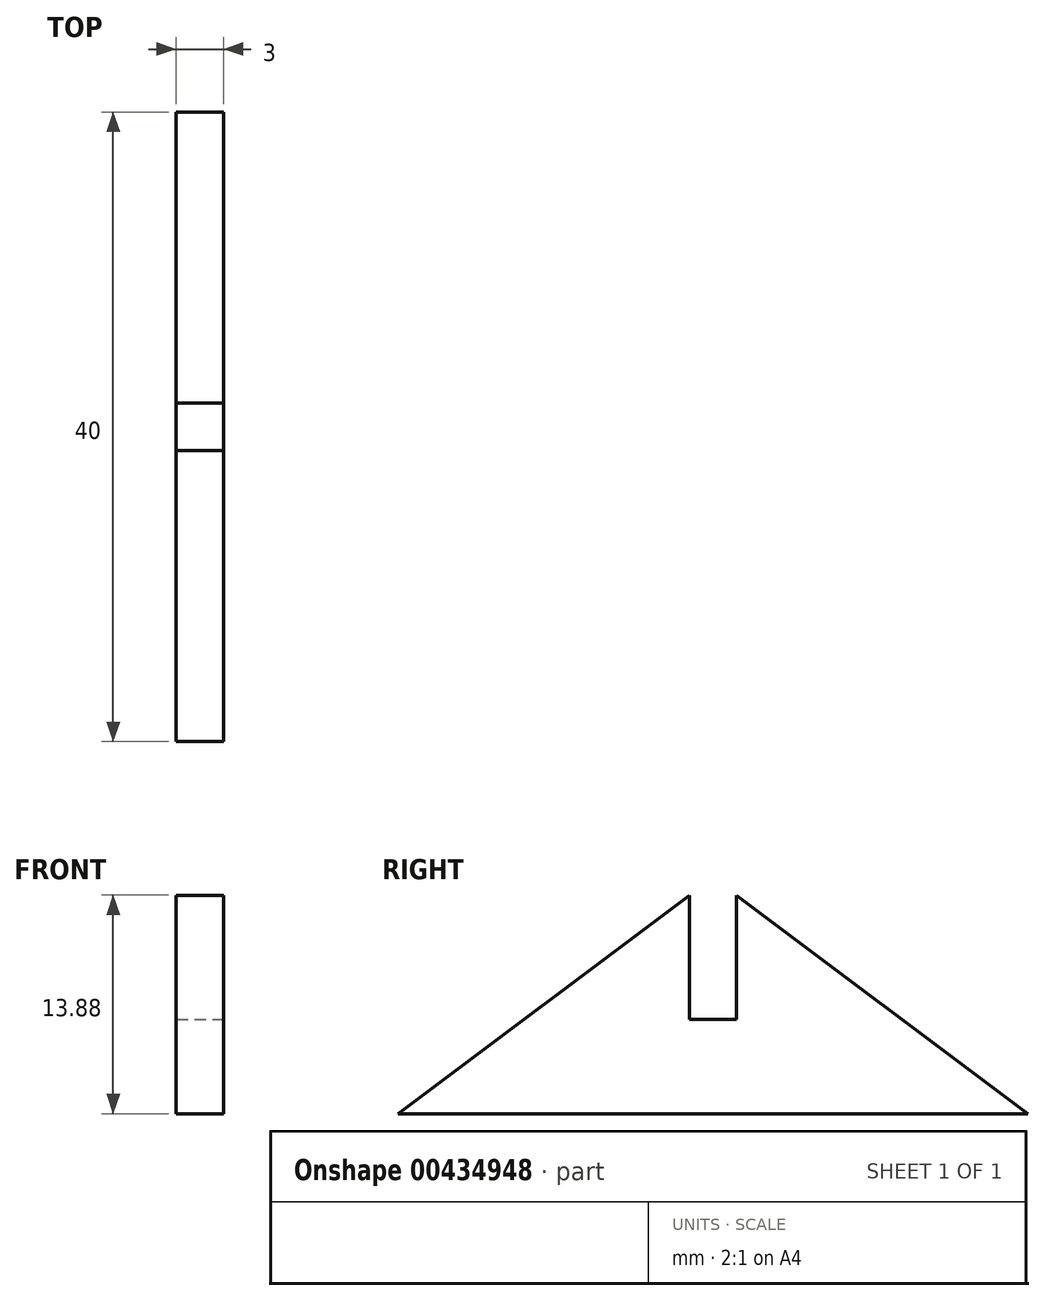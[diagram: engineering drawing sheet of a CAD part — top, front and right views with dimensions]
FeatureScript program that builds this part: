
annotation { "Feature Type Name" : "Feature", "Feature Type Description" : "" }
export const myFeature = defineFeature(function(context is Context, id is Id, definition is map)
    precondition{}
    {
        {
            var Q0;
            Q0=qCreatedBy(makeId("Right.planeOp"),FACE);
            var sketch = newSketch(context, id + "F0", { "sketchPlane" : qUnion([Q0])});
            skLineSegment(sketch, "E0", {"start": v(-20, 0) * mm, "end": v(20, 0) * mm});
            skLineSegment(sketch, "E1", {"start": v(20, 0) * mm, "end": v(0, 15) * mm});
            skLineSegment(sketch, "E2", {"start": v(0, 15) * mm, "end": v(-20, 0) * mm});
            skSolve(sketch);
        }
        {
            var Q0;
            Q0=makeQuery(id+"F0.imprint","IMPRINT",FACE,{"disambiguationData":[TD([[makeQuery(id+"F0.imprint","IMPRINT",EDGE,{"derivedFrom":sQuery(id+"F0.wireOp",EDGE,"E0")}),1.0]])]});
            extrude(context, id + "F1", {"entities" : qUnion([Q0]), "endBound" : BoundingType.SYMMETRIC, "depth" : 3 * mm});
        }
        {
            var Q0;
            Q0=makeQuery(id+"F1.opExtrude","CAP_FACE",FACE,{"disambiguationData":[OSD([sQuery(id+"F0.wireOp",EDGE,"E0"),sQuery(id+"F0.wireOp",EDGE,"E1"),sQuery(id+"F0.wireOp",EDGE,"E2")])],"isStart":false});
            var sketch = newSketch(context, id + "F2", { "sketchPlane" : qUnion([Q0])});
            skLineSegment(sketch, "E3.bottom", {"start": v(-1.5, 6) * mm, "end": v(1.5, 6) * mm});
            skLineSegment(sketch, "E3.top", {"start": v(-1.5, 15) * mm, "end": v(1.5, 15) * mm});
            skLineSegment(sketch, "E3.left", {"start": v(-1.5, 6) * mm, "end": v(-1.5, 15) * mm});
            skLineSegment(sketch, "E3.right", {"start": v(1.5, 6) * mm, "end": v(1.5, 15) * mm});
            skSolve(sketch);
        }
        {
            var Q0;
            {var subQ6=sQuery(id+"F2.wireOp",EDGE,"E3.bottom");Q0=makeQuery(id+"F2.imprint","IMPRINT",FACE,{"disambiguationData":[TD([[makeQuery(id+"F2.imprint","IMPRINT",EDGE,{"derivedFrom":subQ6}),1.0]])]});}
            extrude(context, id + "F3", {"entities" : qUnion([Q0]), "operationType" : NewBodyOperationType.REMOVE, "oppositeDirection" : true, "depth" : 25 * mm});
        }
    });
